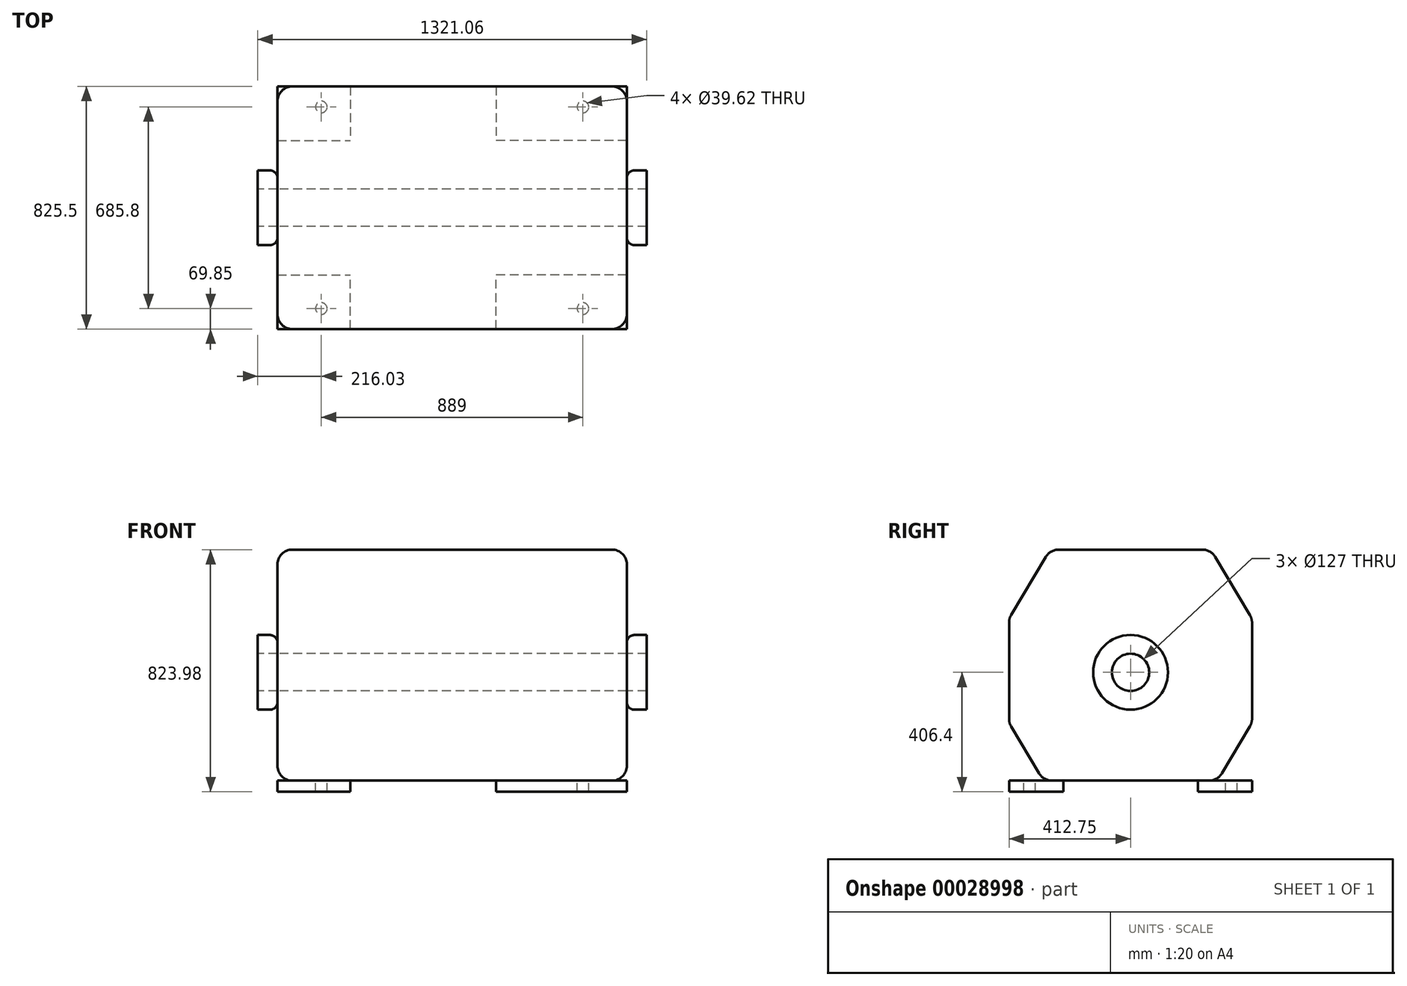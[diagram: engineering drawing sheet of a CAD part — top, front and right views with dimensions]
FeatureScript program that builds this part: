
annotation { "Feature Type Name" : "Feature", "Feature Type Description" : "" }
export const myFeature = defineFeature(function(context is Context, id is Id, definition is map)
    precondition{}
    {
        {
            var Q0;
            Q0=qCreatedBy(makeId("Top.planeOp"),FACE);
            var sketch = newSketch(context, id + "F0", { "sketchPlane" : qUnion([Q0])});
            skLineSegment(sketch, "E0.rect.bottom", {"start": v(-593.73, 412.75) * mm, "end": v(593.73, 412.75) * mm, "construction": true});
            skLineSegment(sketch, "E0.rect.top", {"start": v(-593.73, -412.75) * mm, "end": v(593.73, -412.75) * mm, "construction": true});
            skLineSegment(sketch, "E0.rect.left", {"start": v(-593.72, 412.75) * mm, "end": v(-593.73, -412.75) * mm, "construction": true});
            skLineSegment(sketch, "E0.rect.right", {"start": v(593.73, 412.75) * mm, "end": v(593.73, -412.75) * mm, "construction": true});
            skPoint(sketch, "E0.rect.middle", {"position": v(0, 0) * mm});
            skLineSegment(sketch, "E1", {"start": v(0, 412.75) * mm, "end": v(0, -412.75) * mm, "construction": true});
            skLineSegment(sketch, "E2", {"start": v(-593.73, 0) * mm, "end": v(593.73, 0) * mm, "construction": true});
            skLineSegment(sketch, "E3.bottom", {"start": v(-593.73, 412.75) * mm, "end": v(-346.08, 412.75) * mm});
            skLineSegment(sketch, "E3.top", {"start": v(-593.73, 228.6) * mm, "end": v(-346.08, 228.6) * mm});
            skLineSegment(sketch, "E3.left", {"start": v(-593.73, 412.75) * mm, "end": v(-593.73, 228.6) * mm});
            skLineSegment(sketch, "E3.right", {"start": v(-346.08, 412.75) * mm, "end": v(-346.08, 228.6) * mm});
            skLineSegment(sketch, "E4.bottom", {"start": v(593.73, 412.75) * mm, "end": v(149.23, 412.75) * mm});
            skLineSegment(sketch, "E4.top", {"start": v(593.73, 228.6) * mm, "end": v(149.23, 228.6) * mm});
            skLineSegment(sketch, "E4.left", {"start": v(593.73, 412.75) * mm, "end": v(593.73, 228.6) * mm});
            skLineSegment(sketch, "E4.right", {"start": v(149.23, 412.75) * mm, "end": v(149.23, 228.6) * mm});
            skLineSegment(sketch, "E5.0", {"start": v(-593.73, 342.9) * mm, "end": v(593.73, 342.9) * mm, "construction": true});
            skLineSegment(sketch, "E6.0", {"start": v(-444.5, 412.75) * mm, "end": v(-444.5, -412.75) * mm, "construction": true});
            skCircle(sketch, "E7", {"center": v(-444.5, 342.9) * mm, "radius": 19.81 * mm});
            skCircle(sketch, "E8.MirrorC", {"center": v(444.5, 342.9) * mm, "radius": 19.81 * mm});
            skCircle(sketch, "E9.MirrorC", {"center": v(-444.5, -342.9) * mm, "radius": 19.81 * mm});
            skLineSegment(sketch, "E10.MirrorCS", {"start": v(-593.73, -228.6) * mm, "end": v(-346.08, -228.6) * mm});
            skLineSegment(sketch, "E11.MirrorCS", {"start": v(-593.73, -412.75) * mm, "end": v(-593.73, -228.6) * mm});
            skLineSegment(sketch, "E12.MirrorCS", {"start": v(-346.08, -412.75) * mm, "end": v(-346.08, -228.6) * mm});
            skLineSegment(sketch, "E13.MirrorCS", {"start": v(149.23, -412.75) * mm, "end": v(149.23, -228.6) * mm});
            skCircle(sketch, "E14.MirrorC", {"center": v(444.5, -342.9) * mm, "radius": 19.81 * mm});
            skLineSegment(sketch, "E15.MirrorCS", {"start": v(-593.73, -412.75) * mm, "end": v(593.73, -412.75) * mm});
            skLineSegment(sketch, "E16.MirrorCS", {"start": v(593.73, -228.6) * mm, "end": v(149.23, -228.6) * mm});
            skLineSegment(sketch, "E17.MirrorCS", {"start": v(-593.73, -342.9) * mm, "end": v(593.73, -342.9) * mm, "construction": true});
            skLineSegment(sketch, "E18.MirrorCS", {"start": v(593.73, -412.75) * mm, "end": v(149.23, -412.75) * mm});
            skLineSegment(sketch, "E19.MirrorCS", {"start": v(-593.73, -412.75) * mm, "end": v(-346.08, -412.75) * mm});
            skLineSegment(sketch, "E20.MirrorCS", {"start": v(593.73, -412.75) * mm, "end": v(593.73, -228.6) * mm});
            skSolve(sketch);
        }
        {
            var Q0;
            Q0 = qSketchRegion(id + "F0", true);
            extrude(context, id + "F1", {"entities" : qUnion([Q0]), "oppositeDirection" : true, "depth" : 38.1 * mm});
        }
        {
            var Q0;
            Q0=qCreatedBy(makeId("Right.planeOp"),FACE);
            var sketch = newSketch(context, id + "F2", { "sketchPlane" : qUnion([Q0])});
            skLineSegment(sketch, "E21.0", {"start": v(-228.6, -38.1) * mm, "end": v(-228.6, 0) * mm, "construction": true});
            skLineSegment(sketch, "E22.0", {"start": v(228.6, -38.1) * mm, "end": v(228.6, 0) * mm, "construction": true});
            skLineSegment(sketch, "E23", {"start": v(-228.6, -38.1) * mm, "end": v(228.6, -38.1) * mm, "construction": true});
            skLineSegment(sketch, "E24.0", {"start": v(-228.6, 785.88) * mm, "end": v(412.75, 785.88) * mm, "construction": true});
            skLineSegment(sketch, "E25.0.0", {"start": v(-228.6, 0) * mm, "end": v(-412.75, 0) * mm, "construction": true});
            skLineSegment(sketch, "E25.0.1", {"start": v(-412.75, 0) * mm, "end": v(-412.75, -38.1) * mm, "construction": true});
            skLineSegment(sketch, "E25.0.2", {"start": v(-412.75, -38.1) * mm, "end": v(-228.6, -38.1) * mm, "construction": true});
            skLineSegment(sketch, "E26.0.0", {"start": v(412.75, 0) * mm, "end": v(228.6, 0) * mm, "construction": true});
            skLineSegment(sketch, "E26.0.1", {"start": v(228.6, 0) * mm, "end": v(228.6, -38.1) * mm, "construction": true});
            skLineSegment(sketch, "E26.0.2", {"start": v(228.6, -38.1) * mm, "end": v(412.75, -38.1) * mm, "construction": true});
            skLineSegment(sketch, "E26.0.3", {"start": v(412.75, -38.1) * mm, "end": v(412.75, 785.88) * mm, "construction": true});
            skLineSegment(sketch, "E27.bottom", {"start": v(273.05, 785.88) * mm, "end": v(-273.05, 785.88) * mm});
            skLineSegment(sketch, "E27.top", {"start": v(412.75, 0) * mm, "end": v(-412.75, 0) * mm});
            skLineSegment(sketch, "E27.left", {"start": v(412.75, 785.88) * mm, "end": v(412.75, 196.09) * mm});
            skLineSegment(sketch, "E27.right", {"start": v(-412.75, 551.69) * mm, "end": v(-412.75, 196.09) * mm});
            skLineSegment(sketch, "E28.0", {"start": v(-273.05, 785.88) * mm, "end": v(-273.05, 0) * mm, "construction": true});
            skLineSegment(sketch, "E29", {"start": v(412.75, 373.89) * mm, "end": v(-412.75, 373.89) * mm, "construction": true});
            skLineSegment(sketch, "E30.0", {"start": v(412.75, 551.69) * mm, "end": v(-412.75, 551.69) * mm, "construction": true});
            skLineSegment(sketch, "E31", {"start": v(-412.75, 551.69) * mm, "end": v(-273.05, 785.88) * mm});
            skLineSegment(sketch, "E32.MirrorCS", {"start": v(-412.75, 196.09) * mm, "end": v(-273.05, -38.1) * mm});
            skLineSegment(sketch, "E33", {"start": v(0, 785.88) * mm, "end": v(0, -289.7) * mm, "construction": true});
            skLineSegment(sketch, "E34.MirrorCS", {"start": v(412.75, 551.69) * mm, "end": v(273.05, 785.88) * mm});
            skLineSegment(sketch, "E35.MirrorCS", {"start": v(412.75, 196.09) * mm, "end": v(273.05, -38.1) * mm});
            skPoint(sketch, "E36.orphan", {"position": v(-412.75, 785.88) * mm});
            skSolve(sketch);
        }
        {
            var Q0;
            Q0 = qSketchRegion(id + "F2", true);
            var Q1;
            Q1=makeQuery(id+"F1.opExtrude","SWEPT_FACE",FACE,{"disambiguationData":[OSD([sQuery(id+"F0.wireOp",EDGE,"E20.MirrorCS")])]});
            var Q2;
            Q2=makeQuery(id+"F1.opExtrude","SWEPT_FACE",FACE,{"disambiguationData":[OSD([sQuery(id+"F0.wireOp",EDGE,"E3.left")])]});
            extrude(context, id + "F3", {"entities" : qUnion([Q0]), "endBound" : BoundingType.UP_TO_SURFACE, "endBoundEntityFace" : qUnion([Q1]), "depth" : 25.4 * mm, "hasSecondDirection" : true, "secondDirectionBound" : SecondDirectionBoundingType.UP_TO_SURFACE, "secondDirectionOppositeDirection" : true, "secondDirectionBoundEntityFace" : qUnion([Q2]), "secondDirectionDepth" : 25.4 * mm});
        }
        {
            var Q0;
            Q0=makeQuery(id+"F3.opExtrude","CAP_FACE",FACE,{"disambiguationData":[OSD([sQuery(id+"F2.wireOp",EDGE,"E27.bottom"),sQuery(id+"F2.wireOp",EDGE,"E27.top"),sQuery(id+"F2.wireOp",EDGE,"E27.left"),sQuery(id+"F2.wireOp",EDGE,"E27.right"),sQuery(id+"F2.wireOp",EDGE,"E31"),sQuery(id+"F2.wireOp",EDGE,"E32.MirrorCS"),sQuery(id+"F2.wireOp",EDGE,"E34.MirrorCS"),sQuery(id+"F2.wireOp",EDGE,"E35.MirrorCS")])],"isStart":false});
            var Q1;
            Q1=makeQuery(id+"F3.opExtrude","CAP_FACE",FACE,{"disambiguationData":[OSD([sQuery(id+"F2.wireOp",EDGE,"E27.bottom"),sQuery(id+"F2.wireOp",EDGE,"E27.top"),sQuery(id+"F2.wireOp",EDGE,"E27.left"),sQuery(id+"F2.wireOp",EDGE,"E27.right"),sQuery(id+"F2.wireOp",EDGE,"E31"),sQuery(id+"F2.wireOp",EDGE,"E32.MirrorCS"),sQuery(id+"F2.wireOp",EDGE,"E34.MirrorCS"),sQuery(id+"F2.wireOp",EDGE,"E35.MirrorCS")])],"isStart":true});
            var Q2;
            Q2=makeQuery(id+"F3.opExtrude","SWEPT_FACE",FACE,{"disambiguationData":[OSD([sQuery(id+"F2.wireOp",EDGE,"E35.MirrorCS")])]});
            var Q3;
            Q3=makeQuery(id+"F3.opExtrude","SWEPT_FACE",FACE,{"disambiguationData":[OSD([sQuery(id+"F2.wireOp",EDGE,"E27.left")])]});
            var Q4;
            Q4=makeQuery(id+"F3.opExtrude","SWEPT_FACE",FACE,{"disambiguationData":[OSD([sQuery(id+"F2.wireOp",EDGE,"E34.MirrorCS")])]});
            var Q5;
            Q5=makeQuery(id+"F3.opExtrude","SWEPT_FACE",FACE,{"disambiguationData":[OSD([sQuery(id+"F2.wireOp",EDGE,"E31")])]});
            var Q6;
            Q6=makeQuery(id+"F3.opExtrude","SWEPT_FACE",FACE,{"disambiguationData":[OSD([sQuery(id+"F2.wireOp",EDGE,"E27.right")])]});
            var Q7;
            Q7=makeQuery(id+"F3.opExtrude","SWEPT_FACE",FACE,{"disambiguationData":[OSD([sQuery(id+"F2.wireOp",EDGE,"E32.MirrorCS")])]});
            fillet(context, id + "F4", {"entities" : qUnion([Q0, Q1, Q2, Q3, Q4, Q5, Q6, Q7]), "radius" : 50.8 * mm, "tangentPropagation" : true, "allowEdgeOverflow" : false});
        }
        {
            var Q0;
            Q0=makeQuery(id+"F3.opExtrude","CAP_FACE",FACE,{"disambiguationData":[OSD([sQuery(id+"F2.wireOp",EDGE,"E27.bottom"),sQuery(id+"F2.wireOp",EDGE,"E27.top"),sQuery(id+"F2.wireOp",EDGE,"E27.left"),sQuery(id+"F2.wireOp",EDGE,"E27.right"),sQuery(id+"F2.wireOp",EDGE,"E31"),sQuery(id+"F2.wireOp",EDGE,"E32.MirrorCS"),sQuery(id+"F2.wireOp",EDGE,"E34.MirrorCS"),sQuery(id+"F2.wireOp",EDGE,"E35.MirrorCS")])],"isStart":true});
            var sketch = newSketch(context, id + "F5", { "sketchPlane" : qUnion([Q0])});
            skLineSegment(sketch, "E37", {"start": v(0, 0) * mm, "end": v(0, 911.74) * mm, "construction": true});
            skLineSegment(sketch, "E38.0", {"start": v(-412.75, -38.1) * mm, "end": v(-228.6, -38.1) * mm, "construction": true});
            skLineSegment(sketch, "E39", {"start": v(-228.6, -38.1) * mm, "end": v(229.54, -38.1) * mm, "construction": true});
            skLineSegment(sketch, "E40.0", {"start": v(-228.6, 368.3) * mm, "end": v(229.54, 368.3) * mm, "construction": true});
            skCircle(sketch, "E41", {"center": v(0, 368.3) * mm, "radius": 127 * mm});
            skSolve(sketch);
        }
        {
            var Q0;
            Q0 = qSketchRegion(id + "F5", true);
            extrude(context, id + "F6", {"entities" : qUnion([Q0]), "depth" : 66.8 * mm});
        }
        {
            var Q0;
            Q0=makeQuery(id+"F6.opExtrude","SWEPT_BODY",BODY,{"disambiguationData":[OSD([sQuery(id+"F5.wireOp",EDGE,"E41")])]});
            var Q1;
            Q1=qCreatedBy(makeId("Right.planeOp"),FACE);
            mirror(context, id + "F7", {"entities" : qUnion([Q0]), "mirrorPlane" : qUnion([Q1])});
        }
        {
            var Q0;
            Q0=makeQuery(id+"F7.opPattern","COPY",EDGE,{"derivedFrom":makeQuery(id+"F6.opExtrude","CAP_EDGE",EDGE,{"disambiguationData":[OSD([sQuery(id+"F5.wireOp",EDGE,"E41")])],"isStart":true}),"instanceName":"1"});
            var Q1;
            Q1=makeQuery(id+"F6.opExtrude","CAP_EDGE",EDGE,{"disambiguationData":[OSD([sQuery(id+"F5.wireOp",EDGE,"E41")])],"isStart":true});
            fillet(context, id + "F8", {"entities" : qUnion([Q0, Q1]), "radius" : 25.4 * mm, "tangentPropagation" : true, "allowEdgeOverflow" : false});
        }
        {
            var Q0;
            Q0=makeQuery(id+"F6.opExtrude","CAP_FACE",FACE,{"disambiguationData":[OSD([sQuery(id+"F5.wireOp",EDGE,"E41")])],"isStart":false});
            var sketch = newSketch(context, id + "F9", { "sketchPlane" : qUnion([Q0])});
            skCircle(sketch, "E42", {"center": v(0, 368.3) * mm, "radius": 63.5 * mm});
            skSolve(sketch);
        }
        {
            var Q0;
            Q0 = qSketchRegion(id + "F9", true);
            extrude(context, id + "F10", {"entities" : qUnion([Q0]), "operationType" : NewBodyOperationType.REMOVE, "endBound" : BoundingType.THROUGH_ALL, "oppositeDirection" : true, "depth" : 25.4 * mm});
        }
    });
